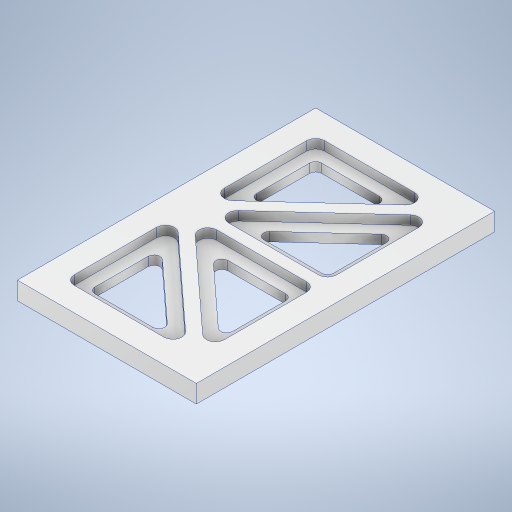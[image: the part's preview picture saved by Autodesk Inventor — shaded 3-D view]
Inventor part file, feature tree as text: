
AUTODESK INVENTOR PART (.ipt)
format: ipt  version: 2024 (Build 280153000, 153)  size: 368,128 bytes
history: native  units: mm
features: projected_geometry x6, extrude x3, fillet x2, sketch x2
ambient origin geometry x8: Origin, YZ Plane, XZ Plane, XY Plane, X Axis, Y Axis, Z Axis, Center Point
bodies: Solid1 (feature_tree)
feature tree (13):
  extrude  "Extrusion1"  Depth=120.0mm
  extrude  "Extrusion2"  Depth=12.0mm
  extrude  "Extrusion3"  Depth=4.0mm
  fillet  "Fillet1"  Radius=4.0mm
  fillet  "Fillet2"  Radius=4.0mm
  sketch  "Sketch1"  dims[d0=200.0mm d1=120.0mm]
  sketch  "Sketch2"  dims[d2=12.0mm d3=0.0mm d4=12.0mm d5=4.0mm d6=4.0mm d7=4.0mm d8=4.0mm d9=4.0mm d10=4.0mm d11=6.0mm d12=0.0mm d13=8.0mm d14=8.0mm d15=8.0mm d16=8.0mm d17=6.0mm d18=0.0mm d19=4.0mm d20=6.0mm]
  projected_geometry  "Projected Loop1"
  projected_geometry  "Projected Loop2"
  projected_geometry  "Projected Loop3"
  projected_geometry  "Projected Loop4"
  projected_geometry  "Projected Loop5"
  projected_geometry  "Projected Loop6"
